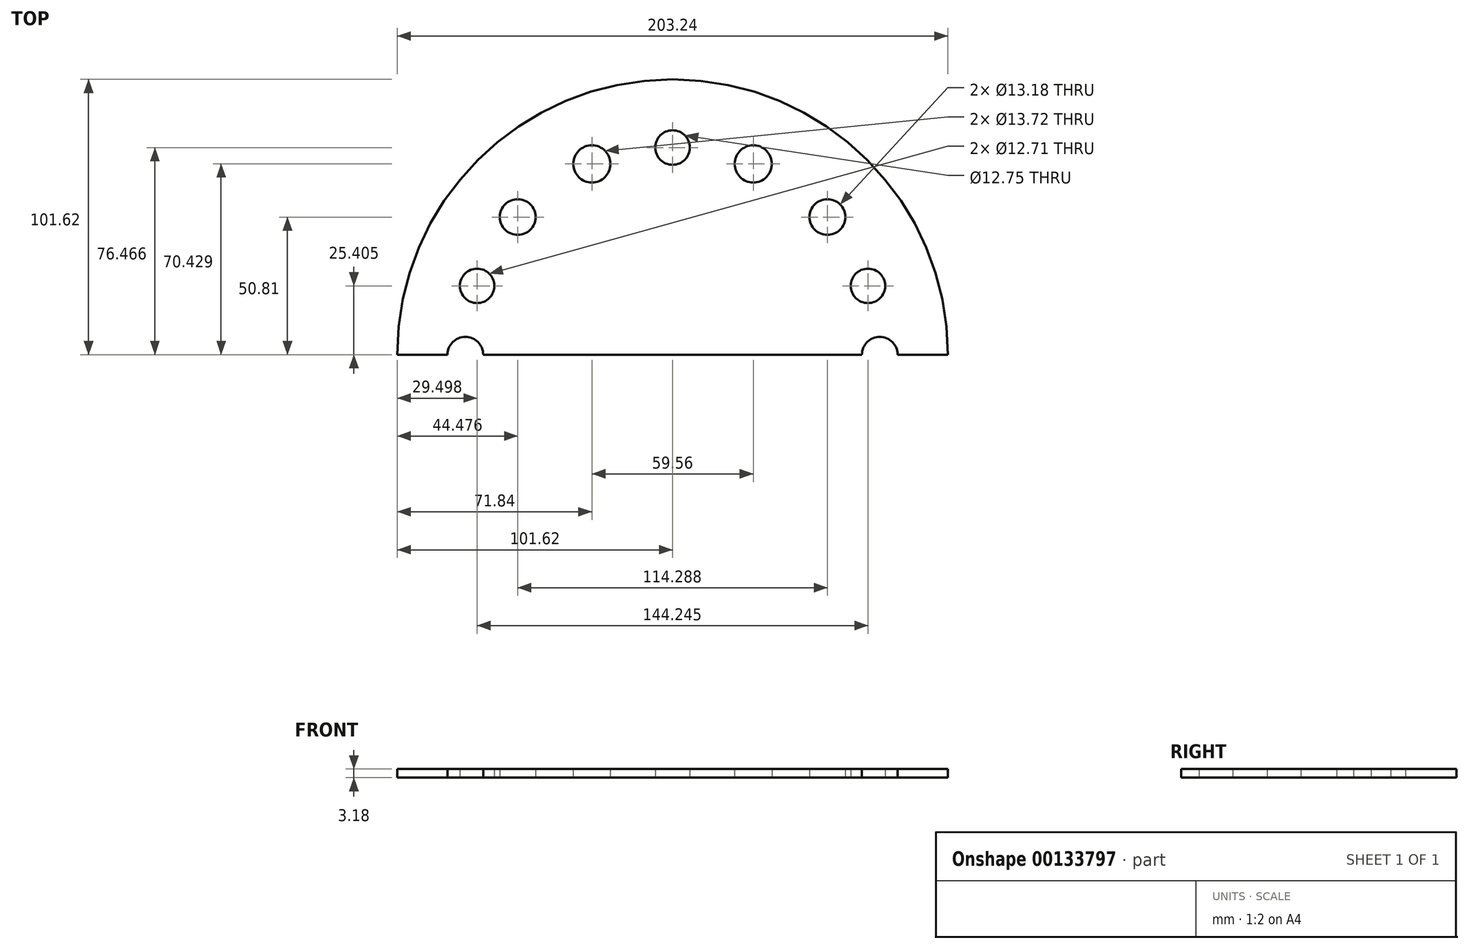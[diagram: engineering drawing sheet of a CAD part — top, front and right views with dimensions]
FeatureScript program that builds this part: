
annotation { "Feature Type Name" : "Feature", "Feature Type Description" : "" }
export const myFeature = defineFeature(function(context is Context, id is Id, definition is map)
    precondition{}
    {
        {
            var Q0;
            Q0=qCreatedBy(makeId("Top.planeOp"),FACE);
            var sketch = newSketch(context, id + "F0", { "sketchPlane" : qUnion([Q0])});
            skCircle(sketch, "E0", {"center": v(0, 0) * mm, "radius": 101.62 * mm});
            skLineSegment(sketch, "E1", {"start": v(0, 0) * mm, "end": v(0, 101.62) * mm});
            skLineSegment(sketch, "E2", {"start": v(0, 0) * mm, "end": v(-101.62, 0) * mm});
            skCircle(sketch, "E3", {"center": v(0, 0) * mm, "radius": 76.47 * mm});
            skLineSegment(sketch, "E4", {"start": v(0, 0) * mm, "end": v(-57.14, 50.8) * mm});
            skPoint(sketch, "E4.endSnap0", {"position": v(0, 50.8) * mm});
            skLineSegment(sketch, "E5", {"start": v(0, 0) * mm, "end": v(-29.78, 70.43) * mm});
            skLineSegment(sketch, "E6", {"start": v(0, 0) * mm, "end": v(-72.12, 25.4) * mm});
            skPoint(sketch, "E6.endSnap0", {"position": v(-28.57, 25.4) * mm});
            skLineSegment(sketch, "E7.MirrorCS", {"start": v(0, 0) * mm, "end": v(29.78, 70.43) * mm});
            skLineSegment(sketch, "E8.MirrorCS", {"start": v(0, 0) * mm, "end": v(57.14, 50.8) * mm});
            skLineSegment(sketch, "E9.MirrorCS", {"start": v(0, 0) * mm, "end": v(72.12, 25.4) * mm});
            skLineSegment(sketch, "E10.MirrorCS", {"start": v(0, 0) * mm, "end": v(101.62, 0) * mm});
            skCircle(sketch, "E11", {"center": v(-72.12, 25.4) * mm, "radius": 6.36 * mm});
            skCircle(sketch, "E12", {"center": v(-57.14, 50.8) * mm, "radius": 6.6 * mm});
            skCircle(sketch, "E13", {"center": v(-29.78, 70.43) * mm, "radius": 6.86 * mm});
            skCircle(sketch, "E14", {"center": v(0, 76.47) * mm, "radius": 6.38 * mm});
            skCircle(sketch, "E15", {"center": v(-76.47, 0) * mm, "radius": 6.57 * mm});
            skCircle(sketch, "E16.MirrorC", {"center": v(29.78, 70.43) * mm, "radius": 6.86 * mm});
            skCircle(sketch, "E17.MirrorC", {"center": v(57.14, 50.8) * mm, "radius": 6.6 * mm});
            skCircle(sketch, "E18.MirrorC", {"center": v(72.12, 25.4) * mm, "radius": 6.36 * mm});
            skCircle(sketch, "E19.MirrorC", {"center": v(76.47, 0) * mm, "radius": 6.57 * mm});
            skSolve(sketch);
        }
        {
            var Q0;
            {var subQ7=sQuery(id+"F0.wireOp",EDGE,"E1");var subQ8=sQuery(id+"F0.wireOp",EDGE,"E0");var subQ9=makeQuery(id+"F0.imprint","INTERSECT",VERTEX,{"derivedFrom":[subQ8,subQ7]});Q0=makeQuery(id+"F0.imprint","IMPRINT",FACE,{"disambiguationData":[TD([[makeQuery(id+"F0.imprint","IMPRINT",EDGE,{"disambiguationData":[TD([[subQ9,-1.0]])],"derivedFrom":subQ8}),1.0]])]});}
            var Q1;
            {var subQ1=sQuery(id+"F0.wireOp",EDGE,"E1");var subQ5=sQuery(id+"F0.wireOp",EDGE,"E0");var subQ6=makeQuery(id+"F0.imprint","INTERSECT",VERTEX,{"derivedFrom":[subQ5,subQ1]});Q1=makeQuery(id+"F0.imprint","IMPRINT",FACE,{"disambiguationData":[TD([[makeQuery(id+"F0.imprint","IMPRINT",EDGE,{"disambiguationData":[TD([[subQ6,1.0]])],"derivedFrom":subQ5}),1.0]])]});}
            var Q2;
            {var subQ3=sQuery(id+"F0.wireOp",EDGE,"E16.MirrorC");var subQ7=sQuery(id+"F0.wireOp",EDGE,"E3");var subQ9=makeQuery(id+"F0.imprint","INTERSECT",VERTEX,{"disambiguationData":[OD(1.0)],"derivedFrom":[subQ7,subQ3]});Q2=makeQuery(id+"F0.imprint","IMPRINT",FACE,{"disambiguationData":[TD([[makeQuery(id+"F0.imprint","IMPRINT",EDGE,{"disambiguationData":[TD([[subQ9,-1.0]])],"derivedFrom":subQ7}),1.0]])]});}
            var Q3;
            {var subQ1=sQuery(id+"F0.wireOp",EDGE,"E3");var subQ5=sQuery(id+"F0.wireOp",EDGE,"E14");var subQ6=makeQuery(id+"F0.imprint","INTERSECT",VERTEX,{"disambiguationData":[OD(1.0)],"derivedFrom":[subQ1,subQ5]});Q3=makeQuery(id+"F0.imprint","IMPRINT",FACE,{"disambiguationData":[TD([[makeQuery(id+"F0.imprint","IMPRINT",EDGE,{"disambiguationData":[TD([[subQ6,-1.0]])],"derivedFrom":subQ1}),1.0]])]});}
            var Q4;
            {var subQ3=sQuery(id+"F0.wireOp",EDGE,"E18.MirrorC");var subQ6=sQuery(id+"F0.wireOp",EDGE,"E3");var subQ9=makeQuery(id+"F0.imprint","INTERSECT",VERTEX,{"disambiguationData":[OD(1.0)],"derivedFrom":[subQ6,subQ3]});Q4=makeQuery(id+"F0.imprint","IMPRINT",FACE,{"disambiguationData":[TD([[makeQuery(id+"F0.imprint","IMPRINT",EDGE,{"disambiguationData":[TD([[subQ9,-1.0]])],"derivedFrom":subQ6}),1.0]])]});}
            var Q5;
            {var subQ1=sQuery(id+"F0.wireOp",EDGE,"E3");var subQ7=sQuery(id+"F0.wireOp",EDGE,"E19.MirrorC");var subQ9=makeQuery(id+"F0.imprint","INTERSECT",VERTEX,{"disambiguationData":[OD(0.0)],"derivedFrom":[subQ1,subQ7]});Q5=makeQuery(id+"F0.imprint","IMPRINT",FACE,{"disambiguationData":[TD([[makeQuery(id+"F0.imprint","IMPRINT",EDGE,{"disambiguationData":[TD([[subQ9,-1.0]])],"derivedFrom":subQ1}),1.0]])]});}
            var Q6;
            {var subQ3=sQuery(id+"F0.wireOp",EDGE,"E13");var subQ7=sQuery(id+"F0.wireOp",EDGE,"E3");var subQ9=makeQuery(id+"F0.imprint","INTERSECT",VERTEX,{"disambiguationData":[OD(1.0)],"derivedFrom":[subQ7,subQ3]});Q6=makeQuery(id+"F0.imprint","IMPRINT",FACE,{"disambiguationData":[TD([[makeQuery(id+"F0.imprint","IMPRINT",EDGE,{"disambiguationData":[TD([[subQ9,-1.0]])],"derivedFrom":subQ7}),1.0]])]});}
            var Q7;
            {var subQ1=sQuery(id+"F0.wireOp",EDGE,"E3");var subQ7=sQuery(id+"F0.wireOp",EDGE,"E12");var subQ9=makeQuery(id+"F0.imprint","INTERSECT",VERTEX,{"disambiguationData":[OD(1.0)],"derivedFrom":[subQ1,subQ7]});Q7=makeQuery(id+"F0.imprint","IMPRINT",FACE,{"disambiguationData":[TD([[makeQuery(id+"F0.imprint","IMPRINT",EDGE,{"disambiguationData":[TD([[subQ9,-1.0]])],"derivedFrom":subQ1}),1.0]])]});}
            var Q8;
            {var subQ3=sQuery(id+"F0.wireOp",EDGE,"E11");var subQ5=sQuery(id+"F0.wireOp",EDGE,"E3");var subQ6=makeQuery(id+"F0.imprint","INTERSECT",VERTEX,{"disambiguationData":[OD(1.0)],"derivedFrom":[subQ5,subQ3]});Q8=makeQuery(id+"F0.imprint","IMPRINT",FACE,{"disambiguationData":[TD([[makeQuery(id+"F0.imprint","IMPRINT",EDGE,{"disambiguationData":[TD([[subQ6,-1.0]])],"derivedFrom":subQ5}),1.0]])]});}
            var Q9;
            {var subQ3=sQuery(id+"F0.wireOp",EDGE,"E17.MirrorC");var subQ6=sQuery(id+"F0.wireOp",EDGE,"E3");var subQ9=makeQuery(id+"F0.imprint","INTERSECT",VERTEX,{"disambiguationData":[OD(1.0)],"derivedFrom":[subQ6,subQ3]});Q9=makeQuery(id+"F0.imprint","IMPRINT",FACE,{"disambiguationData":[TD([[makeQuery(id+"F0.imprint","IMPRINT",EDGE,{"disambiguationData":[TD([[subQ9,-1.0]])],"derivedFrom":subQ6}),1.0]])]});}
            extrude(context, id + "F1", {"entities" : qUnion([Q0, Q1, Q2, Q3, Q4, Q5, Q6, Q7, Q8, Q9]), "depth" : 3.17 * mm});
        }
    });
